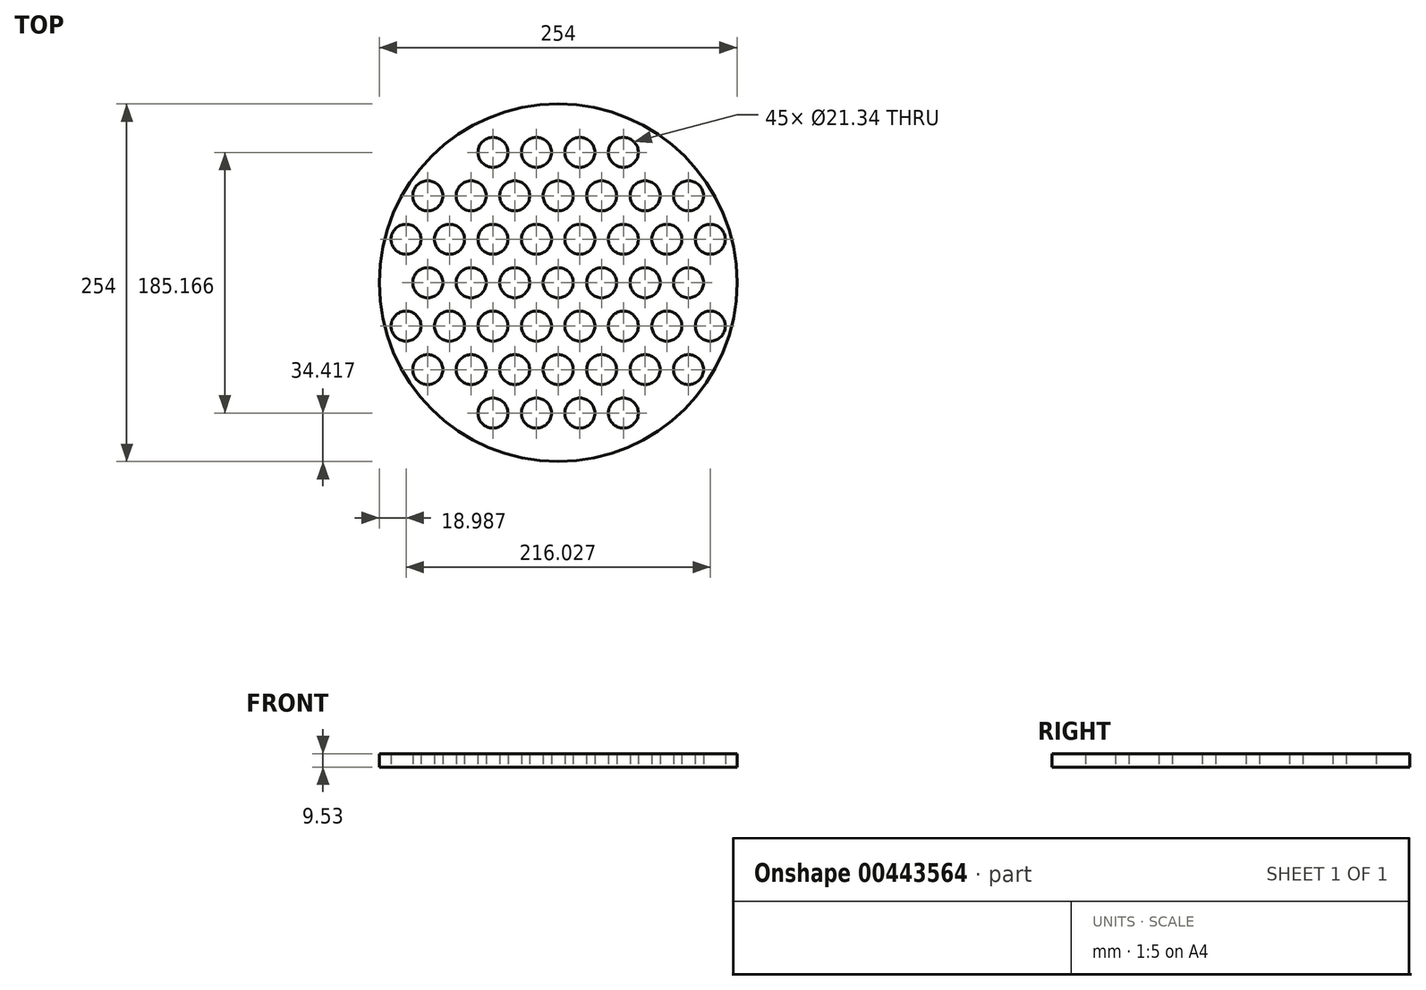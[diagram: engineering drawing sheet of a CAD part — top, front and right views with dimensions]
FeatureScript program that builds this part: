
annotation { "Feature Type Name" : "Feature", "Feature Type Description" : "" }
export const myFeature = defineFeature(function(context is Context, id is Id, definition is map)
    precondition{}
    {
        {
            var Q0;
            Q0=qCreatedBy(makeId("Top.planeOp"),FACE);
            var sketch = newSketch(context, id + "F0", { "sketchPlane" : qUnion([Q0])});
            skCircle(sketch, "E0", {"center": v(0, 0) * mm, "radius": 127 * mm});
            skCircle(sketch, "E1", {"center": v(15.43, 30.86) * mm, "radius": 10.67 * mm});
            skCircle(sketch, "E2", {"center": v(46.3, 30.86) * mm, "radius": 10.67 * mm});
            skCircle(sketch, "E3", {"center": v(-15.43, 30.86) * mm, "radius": 10.67 * mm});
            skCircle(sketch, "E4", {"center": v(-77.15, 30.86) * mm, "radius": 10.67 * mm});
            skCircle(sketch, "E5", {"center": v(-46.3, 30.86) * mm, "radius": 10.67 * mm});
            skCircle(sketch, "E6", {"center": v(-108.01, 30.86) * mm, "radius": 10.67 * mm});
            skCircle(sketch, "E7", {"center": v(77.15, 30.86) * mm, "radius": 10.67 * mm});
            skCircle(sketch, "E8", {"center": v(108.01, 30.86) * mm, "radius": 10.67 * mm});
            skCircle(sketch, "E9", {"center": v(0, 61.72) * mm, "radius": 10.67 * mm});
            skCircle(sketch, "E10", {"center": v(30.86, 61.72) * mm, "radius": 10.67 * mm});
            skCircle(sketch, "E11", {"center": v(-30.86, 61.72) * mm, "radius": 10.67 * mm});
            skCircle(sketch, "E12", {"center": v(-92.58, 61.72) * mm, "radius": 10.67 * mm});
            skCircle(sketch, "E13", {"center": v(-61.72, 61.72) * mm, "radius": 10.67 * mm});
            skCircle(sketch, "E14", {"center": v(61.72, 61.72) * mm, "radius": 10.67 * mm});
            skCircle(sketch, "E15", {"center": v(92.58, 61.72) * mm, "radius": 10.67 * mm});
            skCircle(sketch, "E16", {"center": v(-15.43, 92.58) * mm, "radius": 10.67 * mm});
            skCircle(sketch, "E17", {"center": v(15.43, 92.58) * mm, "radius": 10.67 * mm});
            skCircle(sketch, "E18", {"center": v(-46.3, 92.58) * mm, "radius": 10.67 * mm});
            skCircle(sketch, "E19", {"center": v(46.3, 92.58) * mm, "radius": 10.67 * mm});
            skCircle(sketch, "E20", {"center": v(30.86, -61.72) * mm, "radius": 10.67 * mm});
            skCircle(sketch, "E21", {"center": v(61.72, -61.72) * mm, "radius": 10.67 * mm});
            skCircle(sketch, "E22", {"center": v(0, -61.72) * mm, "radius": 10.67 * mm});
            skCircle(sketch, "E23", {"center": v(-61.72, -61.72) * mm, "radius": 10.67 * mm});
            skCircle(sketch, "E24", {"center": v(-30.86, -61.72) * mm, "radius": 10.67 * mm});
            skCircle(sketch, "E25", {"center": v(-92.58, -61.72) * mm, "radius": 10.67 * mm});
            skCircle(sketch, "E26", {"center": v(92.58, -61.72) * mm, "radius": 10.67 * mm});
            skCircle(sketch, "E27", {"center": v(15.43, -30.86) * mm, "radius": 10.67 * mm});
            skCircle(sketch, "E28", {"center": v(46.3, -30.86) * mm, "radius": 10.67 * mm});
            skCircle(sketch, "E29", {"center": v(-15.43, -30.86) * mm, "radius": 10.67 * mm});
            skCircle(sketch, "E30", {"center": v(-77.15, -30.86) * mm, "radius": 10.67 * mm});
            skCircle(sketch, "E31", {"center": v(-46.3, -30.86) * mm, "radius": 10.67 * mm});
            skCircle(sketch, "E32", {"center": v(-108.01, -30.86) * mm, "radius": 10.67 * mm});
            skCircle(sketch, "E33", {"center": v(77.15, -30.86) * mm, "radius": 10.67 * mm});
            skCircle(sketch, "E34", {"center": v(108.01, -30.86) * mm, "radius": 10.67 * mm});
            skCircle(sketch, "E35", {"center": v(0, 0) * mm, "radius": 10.67 * mm});
            skCircle(sketch, "E36", {"center": v(30.86, 0) * mm, "radius": 10.67 * mm});
            skCircle(sketch, "E37", {"center": v(-30.86, 0) * mm, "radius": 10.67 * mm});
            skCircle(sketch, "E38", {"center": v(-92.58, 0) * mm, "radius": 10.67 * mm});
            skCircle(sketch, "E39", {"center": v(-61.72, 0) * mm, "radius": 10.67 * mm});
            skCircle(sketch, "E40", {"center": v(61.72, 0) * mm, "radius": 10.67 * mm});
            skCircle(sketch, "E41", {"center": v(92.58, 0) * mm, "radius": 10.67 * mm});
            skCircle(sketch, "E42", {"center": v(15.43, -92.58) * mm, "radius": 10.67 * mm});
            skCircle(sketch, "E43", {"center": v(46.3, -92.58) * mm, "radius": 10.67 * mm});
            skCircle(sketch, "E44", {"center": v(-15.43, -92.58) * mm, "radius": 10.67 * mm});
            skCircle(sketch, "E45", {"center": v(-46.3, -92.58) * mm, "radius": 10.67 * mm});
            skSolve(sketch);
        }
        {
            var Q0;
            Q0 = qSketchRegion(id + "F0", true);
            extrude(context, id + "F1", {"entities" : qUnion([Q0]), "depth" : 9.52 * mm});
        }
    });
